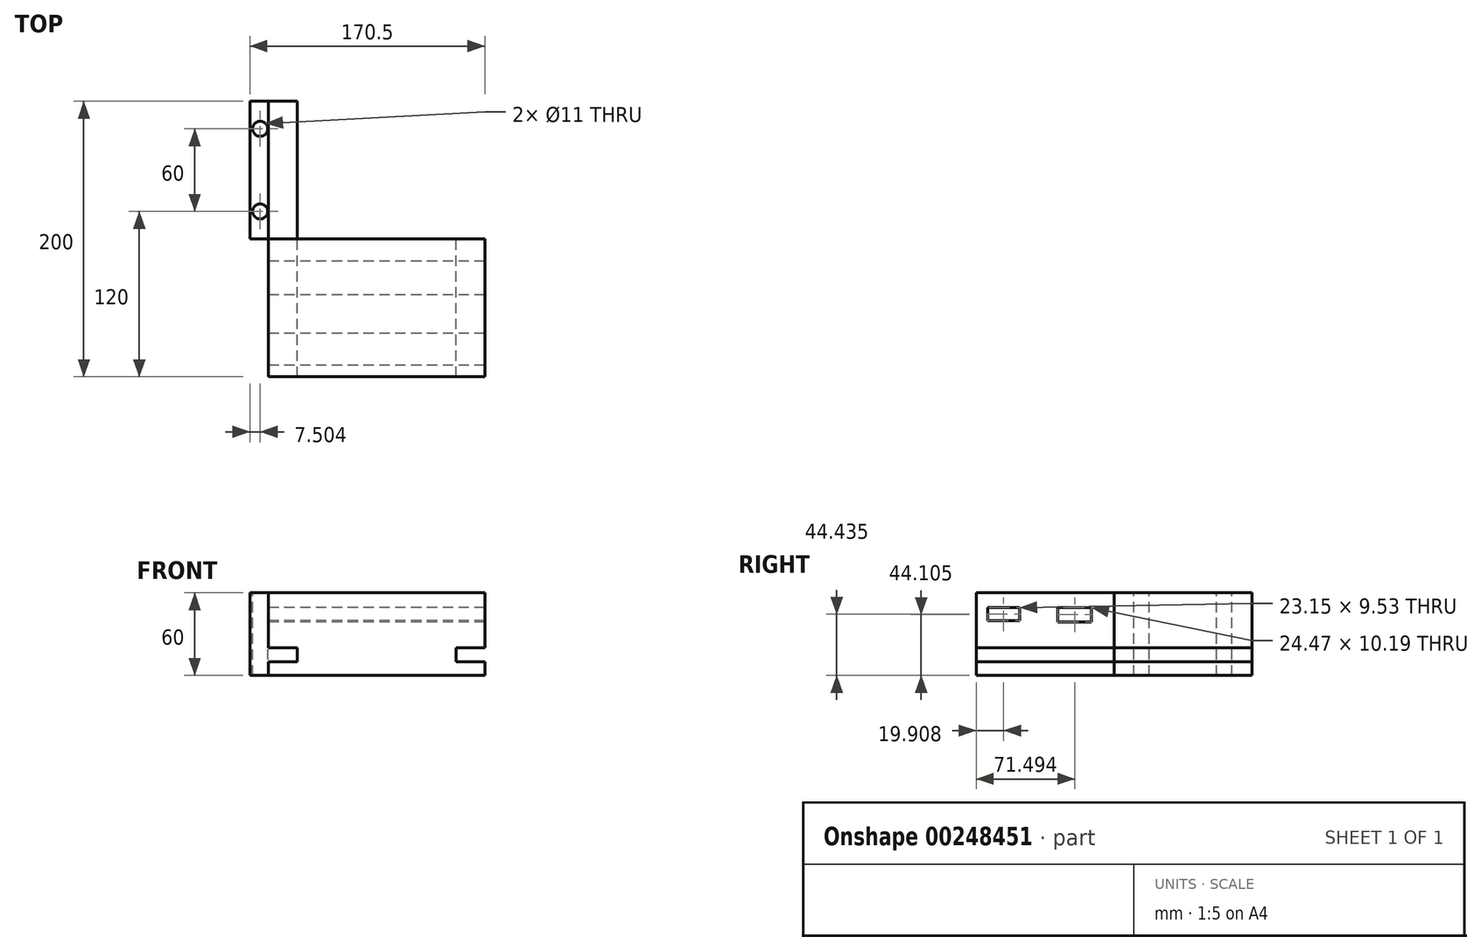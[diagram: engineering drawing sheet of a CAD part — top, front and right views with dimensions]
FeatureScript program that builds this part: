
annotation { "Feature Type Name" : "Feature", "Feature Type Description" : "" }
export const myFeature = defineFeature(function(context is Context, id is Id, definition is map)
    precondition{}
    {
        {
            var Q0;
            Q0=qCreatedBy(makeId("Front.planeOp"),FACE);
            var sketch = newSketch(context, id + "F0", { "sketchPlane" : qUnion([Q0])});
            skLineSegment(sketch, "E0", {"start": v(73.86, 10.8) * mm, "end": v(-83.28, 10.8) * mm});
            skLineSegment(sketch, "E1", {"start": v(-83.28, 10.8) * mm, "end": v(-83.28, -29.2) * mm});
            skLineSegment(sketch, "E2", {"start": v(-62.33, -29.2) * mm, "end": v(-62.33, -39.2) * mm});
            skLineSegment(sketch, "E3", {"start": v(-62.33, -39.2) * mm, "end": v(-83.28, -39.2) * mm});
            skLineSegment(sketch, "E4", {"start": v(-83.28, -39.2) * mm, "end": v(-83.28, -49.2) * mm});
            skLineSegment(sketch, "E5", {"start": v(-83.28, -49.2) * mm, "end": v(73.86, -49.2) * mm});
            skLineSegment(sketch, "E6", {"start": v(73.86, -49.2) * mm, "end": v(73.86, -39.2) * mm});
            skLineSegment(sketch, "E7", {"start": v(73.86, -39.2) * mm, "end": v(52.91, -39.2) * mm});
            skLineSegment(sketch, "E8", {"start": v(52.91, -39.2) * mm, "end": v(52.91, -29.2) * mm});
            skLineSegment(sketch, "E9", {"start": v(52.91, -29.2) * mm, "end": v(73.86, -29.2) * mm});
            skLineSegment(sketch, "E10", {"start": v(73.86, -29.2) * mm, "end": v(73.86, 10.8) * mm});
            skLineSegment(sketch, "E11", {"start": v(-62.33, -29.2) * mm, "end": v(-83.28, -29.2) * mm});
            skSolve(sketch);
        }
        {
            var Q0;
            Q0=makeQuery(id+"F0.imprint","IMPRINT",FACE,{"disambiguationData":[TD([[makeQuery(id+"F0.imprint","IMPRINT",EDGE,{"derivedFrom":sQuery(id+"F0.wireOp",EDGE,"E0")}),1.0]])]});
            extrude(context, id + "F1", {"entities" : qUnion([Q0]), "depth" : 100 * mm});
        }
        {
            var Q0;
            Q0=makeQuery(id+"F1.opExtrude","CAP_FACE",FACE,{"disambiguationData":[OSD([sQuery(id+"F0.wireOp",EDGE,"E0"),sQuery(id+"F0.wireOp",EDGE,"E1"),sQuery(id+"F0.wireOp",EDGE,"E2"),sQuery(id+"F0.wireOp",EDGE,"E3"),sQuery(id+"F0.wireOp",EDGE,"E4"),sQuery(id+"F0.wireOp",EDGE,"E5"),sQuery(id+"F0.wireOp",EDGE,"E6"),sQuery(id+"F0.wireOp",EDGE,"E7"),sQuery(id+"F0.wireOp",EDGE,"E8"),sQuery(id+"F0.wireOp",EDGE,"E9"),sQuery(id+"F0.wireOp",EDGE,"E10"),sQuery(id+"F0.wireOp",EDGE,"E11")])],"isStart":true});
            var sketch = newSketch(context, id + "F2", { "sketchPlane" : qUnion([Q0])});
            skLineSegment(sketch, "E12", {"start": v(83.28, 10.8) * mm, "end": v(96.64, 10.8) * mm});
            skLineSegment(sketch, "E13", {"start": v(96.64, 10.8) * mm, "end": v(96.64, -49.2) * mm});
            skLineSegment(sketch, "E14", {"start": v(83.28, -49.2) * mm, "end": v(96.64, -49.2) * mm});
            skLineSegment(sketch, "E15", {"start": v(83.28, -39.2) * mm, "end": v(62.33, -39.2) * mm});
            skLineSegment(sketch, "E16", {"start": v(62.33, -39.2) * mm, "end": v(62.33, -29.2) * mm});
            skLineSegment(sketch, "E17", {"start": v(62.33, -29.2) * mm, "end": v(83.28, -29.2) * mm});
            skLineSegment(sketch, "E18", {"start": v(83.28, -29.2) * mm, "end": v(83.28, 10.8) * mm});
            skSolve(sketch);
        }
        {
            var Q0;
            Q0=makeQuery(id+"F2.imprint","IMPRINT",FACE,{"disambiguationData":[TD([[makeQuery(id+"F2.imprint","IMPRINT",EDGE,{"derivedFrom":sQuery(id+"F2.wireOp",EDGE,"E12")}),-1.0]])]});
            extrude(context, id + "F3", {"entities" : qUnion([Q0]), "depth" : 100 * mm});
        }
        {
            var Q0;
            Q0=makeQuery(id+"F1.opExtrude","SWEPT_FACE",FACE,{"disambiguationData":[OSD([sQuery(id+"F0.wireOp",EDGE,"E1")])]});
            var sketch = newSketch(context, id + "F4", { "sketchPlane" : qUnion([Q0])});
            skLineSegment(sketch, "E19.bottom", {"start": v(16.27, 0) * mm, "end": v(40.74, 0) * mm});
            skLineSegment(sketch, "E19.top", {"start": v(16.27, -10.2) * mm, "end": v(40.74, -10.2) * mm});
            skLineSegment(sketch, "E19.left", {"start": v(16.27, 0) * mm, "end": v(16.27, -10.2) * mm});
            skLineSegment(sketch, "E19.right", {"start": v(40.74, 0) * mm, "end": v(40.74, -10.2) * mm});
            skLineSegment(sketch, "E20.bottom", {"start": v(68.52, 0) * mm, "end": v(91.67, 0) * mm});
            skLineSegment(sketch, "E20.top", {"start": v(68.52, -9.53) * mm, "end": v(91.67, -9.53) * mm});
            skLineSegment(sketch, "E20.left", {"start": v(68.52, 0) * mm, "end": v(68.52, -9.53) * mm});
            skLineSegment(sketch, "E20.right", {"start": v(91.67, 0) * mm, "end": v(91.67, -9.53) * mm});
            skSolve(sketch);
        }
        {
            var Q0;
            Q0 = qSketchRegion(id + "F4", true);
            extrude(context, id + "F5", {"entities" : qUnion([Q0]), "operationType" : NewBodyOperationType.REMOVE, "endBound" : BoundingType.THROUGH_ALL, "oppositeDirection" : true, "depth" : 25 * mm});
        }
        {
            var Q0;
            Q0=makeQuery(id+"F3.opExtrude","SWEPT_FACE",FACE,{"disambiguationData":[OSD([sQuery(id+"F2.wireOp",EDGE,"E12")])]});
            var sketch = newSketch(context, id + "F6", { "sketchPlane" : qUnion([Q0])});
            skCircle(sketch, "E21", {"center": v(-89.14, 80) * mm, "radius": 5.5 * mm});
            skCircle(sketch, "E22", {"center": v(-89.14, 20) * mm, "radius": 5.5 * mm});
            skSolve(sketch);
        }
        {
            var Q0;
            Q0 = qSketchRegion(id + "F6", true);
            extrude(context, id + "F7", {"entities" : qUnion([Q0]), "operationType" : NewBodyOperationType.REMOVE, "endBound" : BoundingType.THROUGH_ALL, "oppositeDirection" : true, "depth" : 25 * mm});
        }
    });
